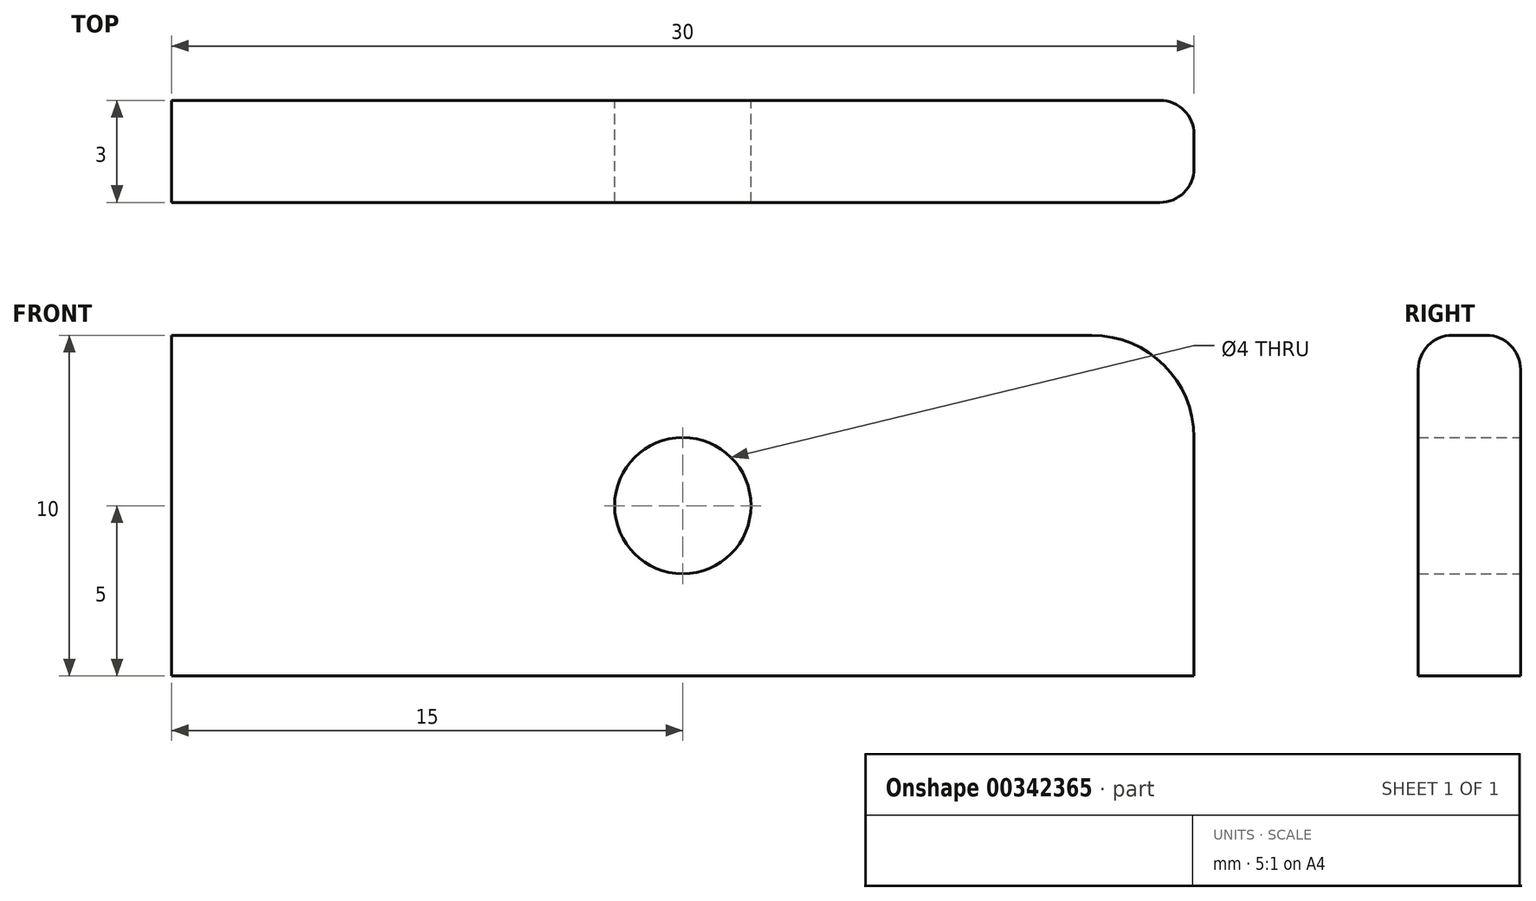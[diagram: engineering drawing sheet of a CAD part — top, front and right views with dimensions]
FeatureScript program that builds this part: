
annotation { "Feature Type Name" : "Feature", "Feature Type Description" : "" }
export const myFeature = defineFeature(function(context is Context, id is Id, definition is map)
    precondition{}
    {
        {
            var Q0;
            Q0=qCreatedBy(makeId("Front.planeOp"),FACE);
            var sketch = newSketch(context, id + "F0", { "sketchPlane" : qUnion([Q0])});
            skLineSegment(sketch, "E0.bottom", {"start": v(-3, 0) * mm, "end": v(-30, 0) * mm});
            skLineSegment(sketch, "E0.top", {"start": v(0, -10) * mm, "end": v(-30, -10) * mm});
            skLineSegment(sketch, "E0.left", {"start": v(0, -3) * mm, "end": v(0, -10) * mm});
            skLineSegment(sketch, "E0.right", {"start": v(-30, 0) * mm, "end": v(-30, -10) * mm});
            skCircle(sketch, "E1", {"center": v(-15, -5) * mm, "radius": 2 * mm});
            skPoint(sketch, "E1.centerSnap0", {"position": v(-15, -10) * mm});
            skPoint(sketch, "E2.visualSharp", {"position": v(0, 0) * mm});
            skArc(sketch, "E2.filletArc", {"start": v(0, -3) * mm, "mid": v(-0.88, -0.88) * mm, "end": v(-3, 0) * mm});
            skSolve(sketch);
        }
        {
            var Q0;
            Q0=makeQuery(id+"F0.imprint","IMPRINT",FACE,{"disambiguationData":[TD([[makeQuery(id+"F0.imprint","IMPRINT",EDGE,{"derivedFrom":sQuery(id+"F0.wireOp",EDGE,"E0.bottom")}),1.0]])]});
            extrude(context, id + "F1", {"entities" : qUnion([Q0]), "depth" : 3 * mm});
        }
        {
            var Q0;
            Q0=makeQuery(id+"F1.opExtrude","CAP_EDGE",EDGE,{"disambiguationData":[OSD([sQuery(id+"F0.wireOp",EDGE,"E0.bottom")])],"isStart":false});
            var Q1;
            Q1=makeQuery(id+"F1.opExtrude","CAP_EDGE",EDGE,{"disambiguationData":[OSD([sQuery(id+"F0.wireOp",EDGE,"E0.bottom")])],"isStart":true});
            fillet(context, id + "F2", {"entities" : qUnion([Q0, Q1]), "radius" : 1 * mm, "tangentPropagation" : true, "allowEdgeOverflow" : false});
        }
    });
